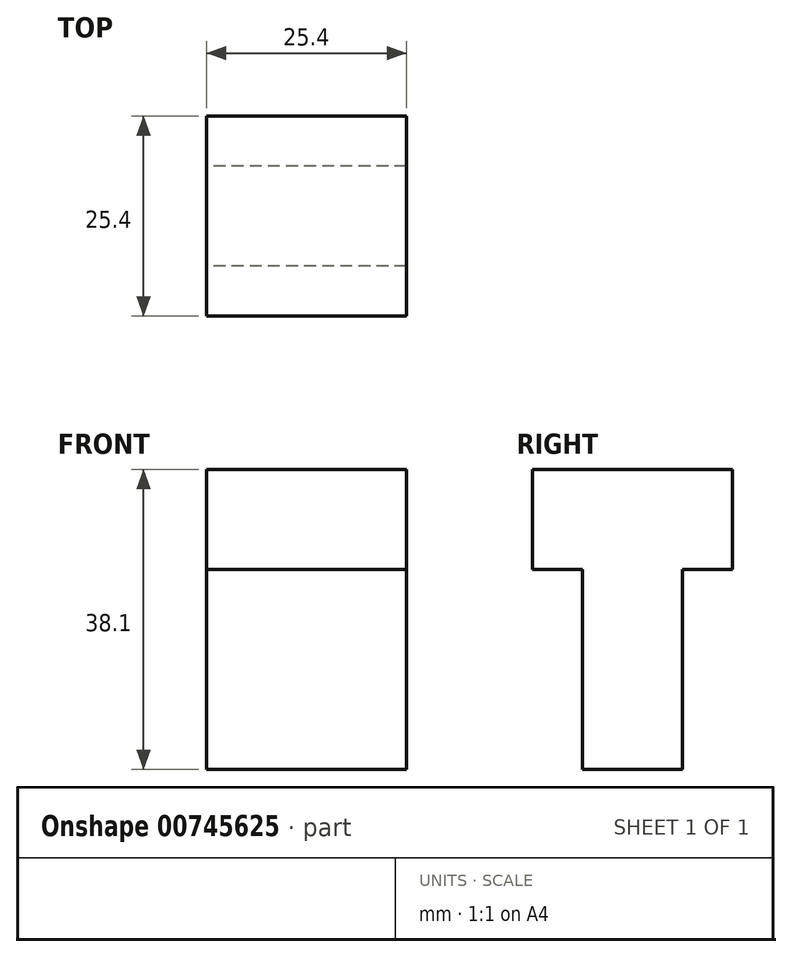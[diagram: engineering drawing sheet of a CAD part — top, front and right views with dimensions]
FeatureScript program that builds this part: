
annotation { "Feature Type Name" : "Feature", "Feature Type Description" : "" }
export const myFeature = defineFeature(function(context is Context, id is Id, definition is map)
    precondition{}
    {
        {
            var Q0;
            Q0=qCreatedBy(makeId("Right.planeOp"),FACE);
            var sketch = newSketch(context, id + "F0", { "sketchPlane" : qUnion([Q0])});
            skLineSegment(sketch, "E0", {"start": v(0, 38.1) * mm, "end": v(0, 25.4) * mm});
            skLineSegment(sketch, "E1", {"start": v(0, 25.4) * mm, "end": v(6.35, 25.4) * mm});
            skLineSegment(sketch, "E2", {"start": v(6.35, 25.4) * mm, "end": v(6.35, 0) * mm});
            skLineSegment(sketch, "E3", {"start": v(6.35, 0) * mm, "end": v(19.05, 0) * mm});
            skLineSegment(sketch, "E4", {"start": v(19.05, 0) * mm, "end": v(19.05, 25.4) * mm});
            skLineSegment(sketch, "E5", {"start": v(19.05, 25.4) * mm, "end": v(25.4, 25.4) * mm});
            skLineSegment(sketch, "E6", {"start": v(25.4, 25.4) * mm, "end": v(25.4, 38.1) * mm});
            skLineSegment(sketch, "E7", {"start": v(25.4, 38.1) * mm, "end": v(0, 38.1) * mm});
            skSolve(sketch);
        }
        {
            var Q0;
            Q0 = qSketchRegion(id + "F0", true);
            extrude(context, id + "F1", {"entities" : qUnion([Q0]), "depth" : 25.4 * mm, "offsetDistance" : 25.4 * mm});
        }
    });
